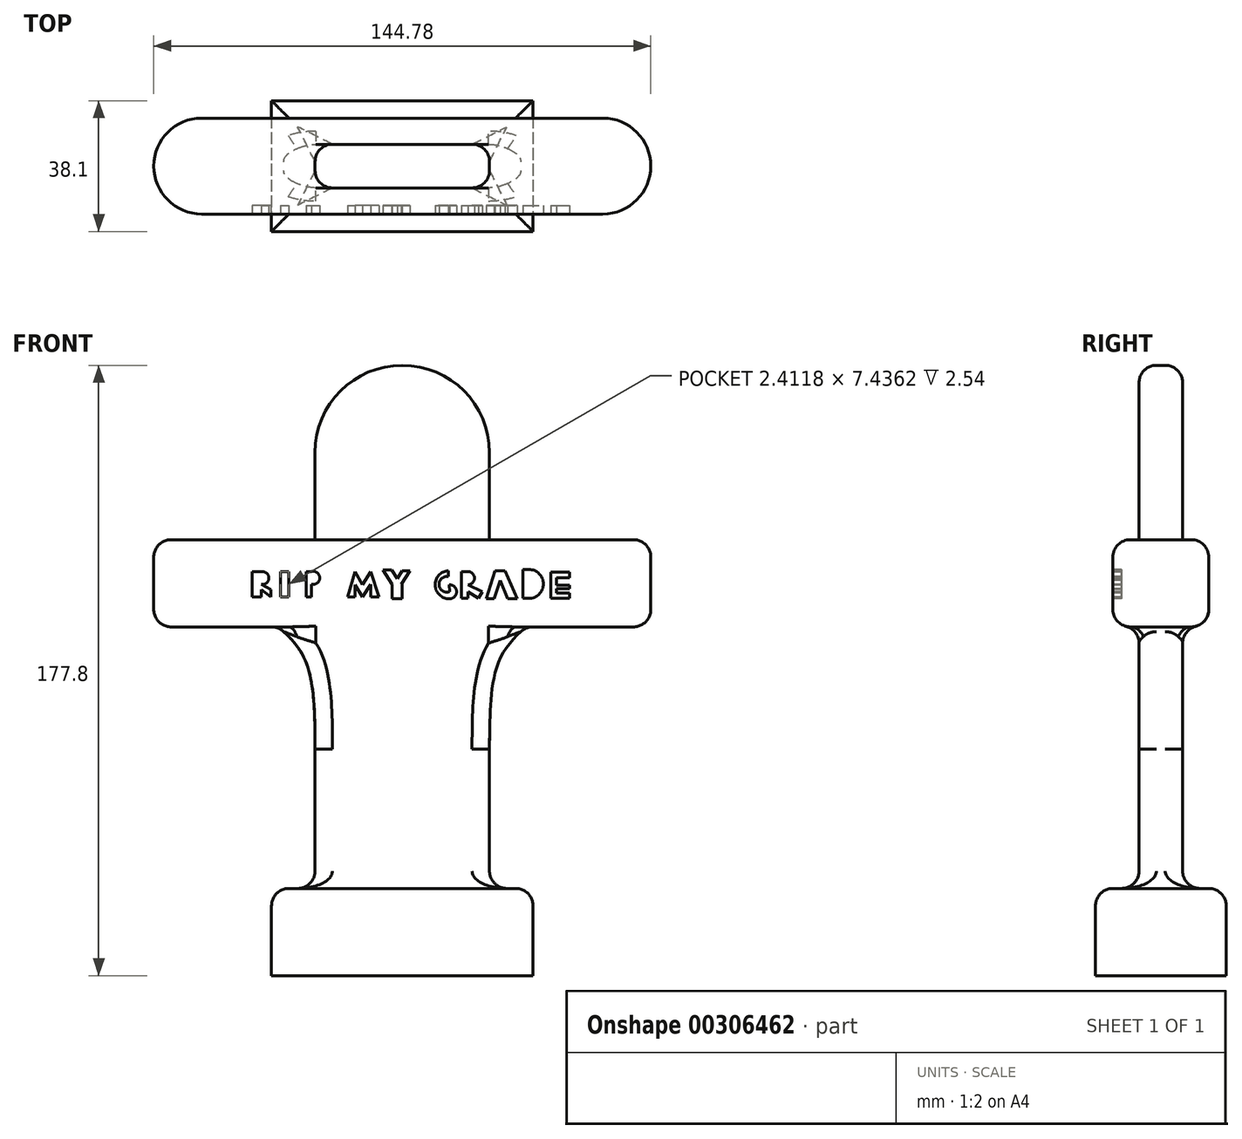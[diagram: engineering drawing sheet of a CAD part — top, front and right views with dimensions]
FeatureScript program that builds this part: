
annotation { "Feature Type Name" : "Feature", "Feature Type Description" : "" }
export const myFeature = defineFeature(function(context is Context, id is Id, definition is map)
    precondition{}
    {
        {
            var Q0;
            Q0=qCreatedBy(makeId("Top.planeOp"),FACE);
            var sketch = newSketch(context, id + "F0", { "sketchPlane" : qUnion([Q0])});
            skLineSegment(sketch, "E0.bottom", {"start": v(-31.32, 7.9) * mm, "end": v(44.88, 7.9) * mm});
            skLineSegment(sketch, "E0.top", {"start": v(-31.32, -30.2) * mm, "end": v(44.88, -30.2) * mm});
            skLineSegment(sketch, "E0.left", {"start": v(-31.32, 7.9) * mm, "end": v(-31.32, -30.2) * mm});
            skLineSegment(sketch, "E0.right", {"start": v(44.88, 7.9) * mm, "end": v(44.88, -30.2) * mm});
            skLineSegment(sketch, "E1", {"start": v(-31.32, -11.15) * mm, "end": v(-18.62, -11.15) * mm, "construction": true});
            skLineSegment(sketch, "E2", {"start": v(-18.62, 7.9) * mm, "end": v(-18.62, -4.8) * mm, "construction": true});
            skLineSegment(sketch, "E3.bottom", {"start": v(-18.62, -4.8) * mm, "end": v(32.18, -4.8) * mm});
            skLineSegment(sketch, "E3.top", {"start": v(-18.62, -17.5) * mm, "end": v(32.18, -17.5) * mm});
            skLineSegment(sketch, "E3.left", {"start": v(-18.62, -4.8) * mm, "end": v(-18.62, -17.5) * mm});
            skLineSegment(sketch, "E3.right", {"start": v(32.18, -4.8) * mm, "end": v(32.18, -17.5) * mm});
            skLineSegment(sketch, "E4", {"start": v(-15.64, -30.2) * mm, "end": v(-15.64, -17.5) * mm, "construction": true});
            skLineSegment(sketch, "E5", {"start": v(32.18, -11.15) * mm, "end": v(44.88, -11.15) * mm, "construction": true});
            skSolve(sketch);
        }
        {
            var Q0;
            Q0=makeQuery(id+"F0.imprint","IMPRINT",FACE,{"disambiguationData":[TD([[makeQuery(id+"F0.imprint","IMPRINT",EDGE,{"derivedFrom":sQuery(id+"F0.wireOp",EDGE,"E0.bottom")}),-1.0]])]});
            extrude(context, id + "F1", {"entities" : qUnion([Q0]), "depth" : 25.4 * mm});
        }
        {
            var Q0;
            Q0=makeQuery(id+"F0.imprint","IMPRINT",FACE,{"disambiguationData":[TD([[makeQuery(id+"F0.imprint","IMPRINT",EDGE,{"derivedFrom":sQuery(id+"F0.wireOp",EDGE,"E3.bottom")}),-1.0]])]});
            extrude(context, id + "F2", {"entities" : qUnion([Q0]), "operationType" : NewBodyOperationType.ADD, "depth" : 101.6 * mm});
        }
        {
            var Q0;
            Q0=makeQuery(id+"F1.opExtrude","CAP_FACE",FACE,{"disambiguationData":[OSD([sQuery(id+"F0.wireOp",EDGE,"E0.bottom"),sQuery(id+"F0.wireOp",EDGE,"E0.top"),sQuery(id+"F0.wireOp",EDGE,"E0.left"),sQuery(id+"F0.wireOp",EDGE,"E0.right"),sQuery(id+"F0.wireOp",EDGE,"E3.bottom"),sQuery(id+"F0.wireOp",EDGE,"E3.top"),sQuery(id+"F0.wireOp",EDGE,"E3.left"),sQuery(id+"F0.wireOp",EDGE,"E3.right")])],"isStart":false});
            fillet(context, id + "F3", {"entities" : qUnion([Q0]), "radius" : 5.08 * mm, "tangentPropagation" : true, "allowEdgeOverflow" : false});
        }
        {
            var Q0;
            Q0=makeQuery(id+"F2.opExtrude","CAP_FACE",FACE,{"disambiguationData":[OSD([sQuery(id+"F0.wireOp",EDGE,"E3.bottom"),sQuery(id+"F0.wireOp",EDGE,"E3.top"),sQuery(id+"F0.wireOp",EDGE,"E3.left"),sQuery(id+"F0.wireOp",EDGE,"E3.right")])],"isStart":false});
            var sketch = newSketch(context, id + "F4", { "sketchPlane" : qUnion([Q0])});
            skLineSegment(sketch, "E6", {"start": v(6.78, -17.5) * mm, "end": v(6.78, -25.12) * mm, "construction": true});
            skLineSegment(sketch, "E7", {"start": v(-18.62, -11.15) * mm, "end": v(-26.24, -11.15) * mm, "construction": true});
            skLineSegment(sketch, "E8.MirrorCS", {"start": v(32.18, -11.15) * mm, "end": v(39.8, -11.15) * mm, "construction": true});
            skLineSegment(sketch, "E9.MirrorCS", {"start": v(6.78, -4.8) * mm, "end": v(6.78, 2.82) * mm, "construction": true});
            skLineSegment(sketch, "E10.bottom", {"start": v(-26.24, -25.12) * mm, "end": v(39.8, -25.12) * mm});
            skLineSegment(sketch, "E10.top", {"start": v(-26.24, 2.82) * mm, "end": v(39.8, 2.82) * mm});
            skLineSegment(sketch, "E10.left", {"start": v(-26.24, -25.12) * mm, "end": v(-26.24, 2.82) * mm});
            skLineSegment(sketch, "E10.right", {"start": v(39.8, -25.12) * mm, "end": v(39.8, 2.82) * mm});
            skSolve(sketch);
        }
        {
            var Q0;
            Q0 = qSketchRegion(id + "F4", true);
            extrude(context, id + "F5", {"entities" : qUnion([Q0]), "operationType" : NewBodyOperationType.ADD, "depth" : 25.4 * mm});
        }
        {
            var Q0;
            Q0=makeQuery(id+"F5.opExtrude","SWEPT_FACE",FACE,{"disambiguationData":[OSD([sQuery(id+"F4.wireOp",EDGE,"E10.right")])]});
            extrude(context, id + "F6", {"entities" : qUnion([Q0]), "operationType" : NewBodyOperationType.ADD, "depth" : 25.4 * mm});
        }
        {
            var Q0;
            Q0=makeQuery(id+"F5.opExtrude","SWEPT_FACE",FACE,{"disambiguationData":[OSD([sQuery(id+"F4.wireOp",EDGE,"E10.left")])]});
            extrude(context, id + "F7", {"entities" : qUnion([Q0]), "operationType" : NewBodyOperationType.ADD, "depth" : 25.4 * mm});
        }
        {
            var Q0;
            {var subQ0=sQuery(id+"F4.wireOp",EDGE,"E10.left");var subQ1=sQuery(id+"F4.wireOp",EDGE,"E10.right");Q0=makeQuery(id+"F7.boolean.opBoolean","MERGE",FACE,{"derivedFrom":[makeQuery(id+"F6.boolean.opBoolean","MERGE",FACE,{"derivedFrom":[makeQuery(id+"F5.opExtrude","CAP_FACE",FACE,{"disambiguationData":[OSD([sQuery(id+"F4.wireOp",EDGE,"E10.bottom"),sQuery(id+"F4.wireOp",EDGE,"E10.top"),subQ0,subQ1])],"isStart":false}),makeQuery(id+"F6.opExtrude","SWEPT_FACE",FACE,{"disambiguationData":[OSD([subQ1]),TDD([makeQuery(id+"F5.opExtrude","CAP_EDGE",EDGE,{"disambiguationData":[OSD([subQ1])],"isStart":false})])]})]}),makeQuery(id+"F7.opExtrude","SWEPT_FACE",FACE,{"disambiguationData":[OSD([subQ0]),TDD([makeQuery(id+"F5.opExtrude","CAP_EDGE",EDGE,{"disambiguationData":[OSD([subQ0])],"isStart":false})])]})]});}
            var sketch = newSketch(context, id + "F8", { "sketchPlane" : qUnion([Q0])});
            skLineSegment(sketch, "E11.0", {"start": v(-18.62, -4.8) * mm, "end": v(32.18, -4.8) * mm});
            skLineSegment(sketch, "E11.1", {"start": v(32.18, -4.8) * mm, "end": v(32.18, -17.5) * mm});
            skLineSegment(sketch, "E11.2", {"start": v(-18.62, -17.5) * mm, "end": v(32.18, -17.5) * mm});
            skLineSegment(sketch, "E11.3", {"start": v(-18.62, -4.8) * mm, "end": v(-18.62, -17.5) * mm});
            skArc(sketch, "E12", {"start": v(65.2, -25.12) * mm, "mid": v(79.17, -11.15) * mm, "end": v(65.2, 2.82) * mm});
            skArc(sketch, "E13", {"start": v(-51.64, 2.82) * mm, "mid": v(-65.6, -11.15) * mm, "end": v(-51.64, -25.12) * mm});
            skSolve(sketch);
        }
        {
            var Q0;
            Q0=makeQuery(id+"F8.imprint","IMPRINT",FACE,{"disambiguationData":[TD([[makeQuery(id+"F8.imprint","IMPRINT",EDGE,{"derivedFrom":sQuery(id+"F8.wireOp",EDGE,"E11.0")}),-1.0]])]});
            extrude(context, id + "F9", {"entities" : qUnion([Q0]), "operationType" : NewBodyOperationType.ADD, "depth" : 25.4 * mm});
        }
        {
            var Q0;
            Q0=makeQuery(id+"F8.imprint","IMPRINT",FACE,{"disambiguationData":[TD([[makeQuery(id+"F8.imprint","IMPRINT",EDGE,{"derivedFrom":sQuery(id+"F8.wireOp",EDGE,"E12")}),1.0]])]});
            var Q1;
            Q1=makeQuery(id+"F8.imprint","IMPRINT",FACE,{"disambiguationData":[TD([[makeQuery(id+"F8.imprint","IMPRINT",EDGE,{"derivedFrom":sQuery(id+"F8.wireOp",EDGE,"E13")}),1.0]])]});
            extrude(context, id + "F10", {"entities" : qUnion([Q0, Q1]), "operationType" : NewBodyOperationType.ADD, "oppositeDirection" : true, "depth" : 25.4 * mm});
        }
        {
            var Q0;
            {var subQ0=sQuery(id+"F4.wireOp",EDGE,"E10.left");var subQ1=sQuery(id+"F4.wireOp",EDGE,"E10.bottom");var subQ2=sQuery(id+"F4.wireOp",EDGE,"E10.right");Q0=makeQuery(id+"F7.boolean.opBoolean","MERGE",EDGE,{"derivedFrom":[makeQuery(id+"F6.boolean.opBoolean","MERGE",EDGE,{"derivedFrom":[makeQuery(id+"F5.opExtrude","CAP_EDGE",EDGE,{"disambiguationData":[OSD([subQ1])],"isStart":true}),makeQuery(id+"F6.opExtrude","SWEPT_EDGE",EDGE,{"disambiguationData":[OSD([subQ1,subQ2]),TDD([makeQuery(id+"F5.opExtrude","CAP_VERTEX",VERTEX,{"disambiguationData":[OSD([subQ1,subQ2])],"isStart":true})])]})]}),makeQuery(id+"F7.opExtrude","SWEPT_EDGE",EDGE,{"disambiguationData":[OSD([subQ1,subQ0]),TDD([makeQuery(id+"F5.opExtrude","CAP_VERTEX",VERTEX,{"disambiguationData":[OSD([subQ1,subQ0])],"isStart":true})])]})]});}
            var Q1;
            {var subQ0=sQuery(id+"F4.wireOp",EDGE,"E10.left");var subQ1=sQuery(id+"F4.wireOp",EDGE,"E10.bottom");var subQ2=sQuery(id+"F4.wireOp",EDGE,"E10.right");Q1=makeQuery(id+"F7.boolean.opBoolean","MERGE",EDGE,{"derivedFrom":[makeQuery(id+"F6.boolean.opBoolean","MERGE",EDGE,{"derivedFrom":[makeQuery(id+"F5.opExtrude","CAP_EDGE",EDGE,{"disambiguationData":[OSD([subQ1])],"isStart":false}),makeQuery(id+"F6.opExtrude","SWEPT_EDGE",EDGE,{"disambiguationData":[OSD([subQ1,subQ2]),TDD([makeQuery(id+"F5.opExtrude","CAP_VERTEX",VERTEX,{"disambiguationData":[OSD([subQ1,subQ2])],"isStart":false})])]})]}),makeQuery(id+"F7.opExtrude","SWEPT_EDGE",EDGE,{"disambiguationData":[OSD([subQ1,subQ0]),TDD([makeQuery(id+"F5.opExtrude","CAP_VERTEX",VERTEX,{"disambiguationData":[OSD([subQ1,subQ0])],"isStart":false})])]})]});}
            var Q2;
            {var subQ0=sQuery(id+"F4.wireOp",EDGE,"E10.left");var subQ1=sQuery(id+"F4.wireOp",EDGE,"E10.top");var subQ2=sQuery(id+"F4.wireOp",EDGE,"E10.right");Q2=makeQuery(id+"F7.boolean.opBoolean","MERGE",EDGE,{"derivedFrom":[makeQuery(id+"F6.boolean.opBoolean","MERGE",EDGE,{"derivedFrom":[makeQuery(id+"F5.opExtrude","CAP_EDGE",EDGE,{"disambiguationData":[OSD([subQ1])],"isStart":false}),makeQuery(id+"F6.opExtrude","SWEPT_EDGE",EDGE,{"disambiguationData":[OSD([subQ1,subQ2]),TDD([makeQuery(id+"F5.opExtrude","CAP_VERTEX",VERTEX,{"disambiguationData":[OSD([subQ1,subQ2])],"isStart":false})])]})]}),makeQuery(id+"F7.opExtrude","SWEPT_EDGE",EDGE,{"disambiguationData":[OSD([subQ1,subQ0]),TDD([makeQuery(id+"F5.opExtrude","CAP_VERTEX",VERTEX,{"disambiguationData":[OSD([subQ1,subQ0])],"isStart":false})])]})]});}
            var Q3;
            {var subQ0=sQuery(id+"F4.wireOp",EDGE,"E10.left");var subQ1=sQuery(id+"F4.wireOp",EDGE,"E10.top");var subQ2=sQuery(id+"F4.wireOp",EDGE,"E10.right");Q3=makeQuery(id+"F7.boolean.opBoolean","MERGE",EDGE,{"derivedFrom":[makeQuery(id+"F6.boolean.opBoolean","MERGE",EDGE,{"derivedFrom":[makeQuery(id+"F5.opExtrude","CAP_EDGE",EDGE,{"disambiguationData":[OSD([subQ1])],"isStart":true}),makeQuery(id+"F6.opExtrude","SWEPT_EDGE",EDGE,{"disambiguationData":[OSD([subQ1,subQ2]),TDD([makeQuery(id+"F5.opExtrude","CAP_VERTEX",VERTEX,{"disambiguationData":[OSD([subQ1,subQ2])],"isStart":true})])]})]}),makeQuery(id+"F7.opExtrude","SWEPT_EDGE",EDGE,{"disambiguationData":[OSD([subQ1,subQ0]),TDD([makeQuery(id+"F5.opExtrude","CAP_VERTEX",VERTEX,{"disambiguationData":[OSD([subQ1,subQ0])],"isStart":true})])]})]});}
            var Q4;
            Q4=makeQuery(id+"F10.opExtrude","CAP_EDGE",EDGE,{"disambiguationData":[OSD([sQuery(id+"F8.wireOp",EDGE,"E12")])],"isStart":true});
            var Q5;
            Q5=makeQuery(id+"F10.opExtrude","CAP_EDGE",EDGE,{"disambiguationData":[OSD([sQuery(id+"F8.wireOp",EDGE,"E13")])],"isStart":true});
            var Q6;
            Q6=makeQuery(id+"F10.opExtrude","CAP_EDGE",EDGE,{"disambiguationData":[OSD([sQuery(id+"F8.wireOp",EDGE,"E13")])],"isStart":false});
            var Q7;
            Q7=makeQuery(id+"F10.opExtrude","CAP_EDGE",EDGE,{"disambiguationData":[OSD([sQuery(id+"F8.wireOp",EDGE,"E12")])],"isStart":false});
            fillet(context, id + "F11", {"entities" : qUnion([Q0, Q1, Q2, Q3, Q4, Q5, Q6, Q7]), "radius" : 5.08 * mm, "tangentPropagation" : true, "allowEdgeOverflow" : false});
        }
        {
            var Q0;
            Q0=makeQuery(id+"F2.opExtrude","SWEPT_FACE",FACE,{"disambiguationData":[OSD([sQuery(id+"F0.wireOp",EDGE,"E3.bottom")])]});
            var sketch = newSketch(context, id + "F12", { "sketchPlane" : qUnion([Q0])});
            skFitSpline(sketch, "E14", {"points": [v(18.62, 66.04) * mm, v(21.3, 91.45) * mm, v(29.6, 101.9) * mm], "startDerivative": vector(0.24, 49.24) * mm, "endDerivative": vector(22.93, 20.98) * mm});
            skLineSegment(sketch, "E15", {"start": v(29.6, 101.9) * mm, "end": v(18.62, 101.6) * mm});
            skLineSegment(sketch, "E16", {"start": v(18.62, 101.6) * mm, "end": v(18.62, 66.04) * mm});
            skLineSegment(sketch, "E17", {"start": v(-6.78, 101.6) * mm, "end": v(-6.78, 30.48) * mm, "construction": true});
            skFitSpline(sketch, "E18.MirrorCS", {"points": [v(-32.18, 66.04) * mm, v(-34.87, 91.45) * mm, v(-43.16, 101.9) * mm], "startDerivative": vector(-0.24, 49.24) * mm, "endDerivative": vector(-22.93, 20.98) * mm});
            skLineSegment(sketch, "E19.MirrorCS", {"start": v(-43.16, 101.9) * mm, "end": v(-32.18, 101.6) * mm});
            skLineSegment(sketch, "E20.MirrorCS", {"start": v(-32.18, 101.6) * mm, "end": v(-32.18, 66.04) * mm});
            skSolve(sketch);
        }
        {
            var Q0;
            Q0=makeQuery(id+"F12.imprint","IMPRINT",FACE,{"disambiguationData":[TD([[makeQuery(id+"F12.imprint","IMPRINT",EDGE,{"derivedFrom":sQuery(id+"F12.wireOp",EDGE,"E18.MirrorCS")}),-1.0]])]});
            var Q1;
            Q1=makeQuery(id+"F12.imprint","IMPRINT",FACE,{"disambiguationData":[TD([[makeQuery(id+"F12.imprint","IMPRINT",EDGE,{"derivedFrom":sQuery(id+"F12.wireOp",EDGE,"E14")}),1.0]])]});
            extrude(context, id + "F13", {"entities" : qUnion([Q0, Q1]), "operationType" : NewBodyOperationType.ADD, "oppositeDirection" : true, "depth" : 12.7 * mm});
        }
        {
            var Q0;
            Q0=makeQuery(id+"F2.opExtrude","SWEPT_EDGE",EDGE,{"disambiguationData":[OSD([sQuery(id+"F0.wireOp",EDGE,"E3.top"),sQuery(id+"F0.wireOp",EDGE,"E3.left")])]});
            var Q1;
            Q1=makeQuery(id+"F2.opExtrude","SWEPT_EDGE",EDGE,{"disambiguationData":[OSD([sQuery(id+"F0.wireOp",EDGE,"E3.top"),sQuery(id+"F0.wireOp",EDGE,"E3.right")])]});
            var Q2;
            Q2=makeQuery(id+"F2.opExtrude","SWEPT_EDGE",EDGE,{"disambiguationData":[OSD([sQuery(id+"F0.wireOp",EDGE,"E3.bottom"),sQuery(id+"F0.wireOp",EDGE,"E3.left")])]});
            var Q3;
            Q3=makeQuery(id+"F2.opExtrude","SWEPT_EDGE",EDGE,{"disambiguationData":[OSD([sQuery(id+"F0.wireOp",EDGE,"E3.bottom"),sQuery(id+"F0.wireOp",EDGE,"E3.right")])]});
            fillet(context, id + "F14", {"entities" : qUnion([Q0, Q1, Q2, Q3]), "radius" : 5.08 * mm, "tangentPropagation" : true, "allowEdgeOverflow" : false});
        }
        {
            var Q0;
            {var subQ0=sQuery(id+"F4.wireOp",EDGE,"E10.bottom");Q0=makeQuery(id+"F7.boolean.opBoolean","MERGE",FACE,{"derivedFrom":[makeQuery(id+"F6.boolean.opBoolean","MERGE",FACE,{"derivedFrom":[makeQuery(id+"F5.opExtrude","SWEPT_FACE",FACE,{"disambiguationData":[OSD([subQ0])]}),makeQuery(id+"F6.opExtrude","SWEPT_FACE",FACE,{"disambiguationData":[OSD([subQ0,sQuery(id+"F4.wireOp",EDGE,"E10.right")])]})]}),makeQuery(id+"F7.opExtrude","SWEPT_FACE",FACE,{"disambiguationData":[OSD([subQ0,sQuery(id+"F4.wireOp",EDGE,"E10.left")])]})]});}
            var sketch = newSketch(context, id + "F15", { "sketchPlane" : qUnion([Q0])});
            skLineSegment(sketch, "E21", {"start": v(-34.32, 110.29) * mm, "end": v(-34.32, 117.67) * mm});
            skArc(sketch, "E22", {"start": v(-34.32, 113.98) * mm, "mid": v(-32.1, 115.82) * mm, "end": v(-34.32, 117.67) * mm});
            skLineSegment(sketch, "E23.bottom", {"start": v(-28.69, 117.73) * mm, "end": v(-26.27, 117.73) * mm});
            skLineSegment(sketch, "E23.top", {"start": v(-28.69, 110.3) * mm, "end": v(-26.27, 110.3) * mm});
            skLineSegment(sketch, "E23.left", {"start": v(-28.69, 117.73) * mm, "end": v(-28.69, 110.3) * mm});
            skLineSegment(sketch, "E23.right", {"start": v(-26.27, 117.73) * mm, "end": v(-26.27, 110.3) * mm});
            skLineSegment(sketch, "E24.bottom", {"start": v(-34.32, 110.29) * mm, "end": v(-36.93, 110.29) * mm});
            skLineSegment(sketch, "E24.top", {"start": v(-34.32, 117.73) * mm, "end": v(-36.93, 117.73) * mm});
            skLineSegment(sketch, "E24.left", {"start": v(-34.32, 110.29) * mm, "end": v(-34.32, 117.73) * mm});
            skLineSegment(sketch, "E24.right", {"start": v(-36.93, 110.29) * mm, "end": v(-36.93, 117.73) * mm});
            skLineSegment(sketch, "E25.bottom", {"start": v(-21.25, 117.73) * mm, "end": v(-19.64, 117.73) * mm});
            skLineSegment(sketch, "E25.top", {"start": v(-21.25, 110.29) * mm, "end": v(-19.64, 110.29) * mm});
            skLineSegment(sketch, "E25.left", {"start": v(-21.25, 117.73) * mm, "end": v(-21.25, 110.29) * mm});
            skLineSegment(sketch, "E25.right", {"start": v(-19.64, 117.73) * mm, "end": v(-19.64, 110.29) * mm});
            skLineSegment(sketch, "E26", {"start": v(-31.5, 110.29) * mm, "end": v(-31.5, 112.5) * mm});
            skLineSegment(sketch, "E27", {"start": v(-31.5, 112.5) * mm, "end": v(-34.32, 113.98) * mm});
            skArc(sketch, "E28", {"start": v(-19.64, 114.01) * mm, "mid": v(-17.25, 115.87) * mm, "end": v(-19.64, 117.73) * mm});
            skLineSegment(sketch, "E29", {"start": v(-9.2, 110.3) * mm, "end": v(-6.98, 117.73) * mm});
            skLineSegment(sketch, "E30", {"start": v(-6.98, 117.73) * mm, "end": v(-4.77, 113.91) * mm});
            skLineSegment(sketch, "E31", {"start": v(-4.77, 113.91) * mm, "end": v(-2.36, 117.73) * mm});
            skLineSegment(sketch, "E32", {"start": v(-2.36, 117.73) * mm, "end": v(0, 110.29) * mm});
            skLineSegment(sketch, "E33", {"start": v(0, 110.29) * mm, "end": v(-2.36, 110.29) * mm});
            skLineSegment(sketch, "E34", {"start": v(-2.36, 110.29) * mm, "end": v(-2.36, 114.01) * mm});
            skPoint(sketch, "E34.endSnap0", {"position": v(-1.18, 114.01) * mm});
            skLineSegment(sketch, "E35", {"start": v(-2.36, 114.01) * mm, "end": v(-4.77, 110.3) * mm});
            skLineSegment(sketch, "E36", {"start": v(-4.77, 110.3) * mm, "end": v(-6.98, 113.91) * mm});
            skLineSegment(sketch, "E37", {"start": v(-9.2, 110.3) * mm, "end": v(-6.98, 110.3) * mm});
            skLineSegment(sketch, "E38", {"start": v(-6.98, 110.3) * mm, "end": v(-6.98, 113.91) * mm});
            skLineSegment(sketch, "E39", {"start": v(1.16, 118.13) * mm, "end": v(3.87, 114.01) * mm});
            skLineSegment(sketch, "E40", {"start": v(3.87, 114.01) * mm, "end": v(6.49, 114.01) * mm});
            skLineSegment(sketch, "E41", {"start": v(6.49, 114.01) * mm, "end": v(8.96, 117.93) * mm});
            skLineSegment(sketch, "E42", {"start": v(8.96, 117.93) * mm, "end": v(6.79, 117.93) * mm});
            skLineSegment(sketch, "E43", {"start": v(6.79, 117.93) * mm, "end": v(5.31, 115.6) * mm});
            skLineSegment(sketch, "E44", {"start": v(5.31, 115.6) * mm, "end": v(3.64, 118.13) * mm});
            skLineSegment(sketch, "E45", {"start": v(3.64, 118.13) * mm, "end": v(1.16, 118.13) * mm});
            skLineSegment(sketch, "E46.bottom", {"start": v(3.87, 114.01) * mm, "end": v(6.69, 114.01) * mm});
            skLineSegment(sketch, "E46.top", {"start": v(3.87, 109.8) * mm, "end": v(6.69, 109.8) * mm});
            skLineSegment(sketch, "E46.left", {"start": v(3.87, 114.01) * mm, "end": v(3.87, 109.8) * mm});
            skLineSegment(sketch, "E46.right", {"start": v(6.69, 114.01) * mm, "end": v(6.69, 109.8) * mm});
            skArc(sketch, "E47", {"start": v(20.25, 117.93) * mm, "mid": v(16.35, 113.71) * mm, "end": v(20.55, 109.8) * mm});
            skArc(sketch, "E48", {"start": v(20.55, 109.8) * mm, "mid": v(22.6, 111.9) * mm, "end": v(20.42, 113.86) * mm});
            skLineSegment(sketch, "E49", {"start": v(20.25, 117.93) * mm, "end": v(20.25, 116.22) * mm});
            skArc(sketch, "E50", {"start": v(20.25, 116.22) * mm, "mid": v(17.49, 113.82) * mm, "end": v(20.56, 111.83) * mm});
            skLineSegment(sketch, "E51", {"start": v(20.42, 113.86) * mm, "end": v(20.56, 111.83) * mm});
            skLineSegment(sketch, "E52.bottom", {"start": v(24.07, 117.73) * mm, "end": v(25.88, 117.73) * mm});
            skLineSegment(sketch, "E52.top", {"start": v(24.07, 110) * mm, "end": v(25.88, 110) * mm});
            skLineSegment(sketch, "E52.left", {"start": v(24.07, 117.73) * mm, "end": v(24.07, 110) * mm});
            skLineSegment(sketch, "E52.right", {"start": v(25.88, 117.73) * mm, "end": v(25.88, 110) * mm});
            skArc(sketch, "E53", {"start": v(25.88, 113.86) * mm, "mid": v(27.82, 115.8) * mm, "end": v(25.88, 117.73) * mm});
            skLineSegment(sketch, "E54", {"start": v(25.88, 111.83) * mm, "end": v(29, 110) * mm});
            skLineSegment(sketch, "E55", {"start": v(29, 110) * mm, "end": v(30.08, 111.83) * mm});
            skLineSegment(sketch, "E56", {"start": v(30.08, 111.83) * mm, "end": v(25.88, 113.86) * mm});
            skLineSegment(sketch, "E57", {"start": v(31.2, 109.8) * mm, "end": v(33.82, 117.93) * mm});
            skLineSegment(sketch, "E58", {"start": v(33.82, 117.93) * mm, "end": v(36.73, 117.93) * mm});
            skLineSegment(sketch, "E59", {"start": v(36.73, 117.93) * mm, "end": v(40.25, 109.8) * mm});
            skLineSegment(sketch, "E60", {"start": v(40.25, 109.8) * mm, "end": v(37.44, 109.8) * mm});
            skLineSegment(sketch, "E61", {"start": v(37.44, 109.8) * mm, "end": v(35.33, 115.12) * mm});
            skLineSegment(sketch, "E62", {"start": v(35.33, 115.12) * mm, "end": v(33.52, 109.8) * mm});
            skLineSegment(sketch, "E63", {"start": v(33.52, 109.8) * mm, "end": v(31.2, 109.8) * mm});
            skLineSegment(sketch, "E64.bottom", {"start": v(41.86, 118.33) * mm, "end": v(43.67, 118.33) * mm});
            skLineSegment(sketch, "E64.top", {"start": v(41.86, 109.9) * mm, "end": v(43.67, 109.9) * mm});
            skLineSegment(sketch, "E64.left", {"start": v(41.86, 118.33) * mm, "end": v(41.86, 109.9) * mm});
            skLineSegment(sketch, "E64.right", {"start": v(43.67, 118.33) * mm, "end": v(43.67, 109.9) * mm});
            skArc(sketch, "E65", {"start": v(43.67, 109.9) * mm, "mid": v(47.89, 114.11) * mm, "end": v(43.67, 118.33) * mm});
            skLineSegment(sketch, "E66.bottom", {"start": v(50.1, 117.53) * mm, "end": v(51.7, 117.53) * mm});
            skLineSegment(sketch, "E66.top", {"start": v(50.1, 110) * mm, "end": v(51.7, 110) * mm});
            skLineSegment(sketch, "E66.left", {"start": v(50.1, 117.53) * mm, "end": v(50.1, 110) * mm});
            skLineSegment(sketch, "E66.right", {"start": v(51.7, 117.53) * mm, "end": v(51.7, 110) * mm});
            skLineSegment(sketch, "E67.bottom", {"start": v(51.7, 110) * mm, "end": v(55.53, 110) * mm});
            skLineSegment(sketch, "E67.top", {"start": v(51.7, 111.4) * mm, "end": v(55.53, 111.4) * mm});
            skLineSegment(sketch, "E67.left", {"start": v(51.7, 110) * mm, "end": v(51.7, 111.4) * mm});
            skLineSegment(sketch, "E67.right", {"start": v(55.53, 110) * mm, "end": v(55.53, 111.4) * mm});
            skLineSegment(sketch, "E68.bottom", {"start": v(51.7, 117.53) * mm, "end": v(55.53, 117.53) * mm});
            skLineSegment(sketch, "E68.top", {"start": v(51.7, 115.92) * mm, "end": v(55.53, 115.92) * mm});
            skLineSegment(sketch, "E68.left", {"start": v(51.7, 117.53) * mm, "end": v(51.7, 115.92) * mm});
            skLineSegment(sketch, "E68.right", {"start": v(55.53, 117.53) * mm, "end": v(55.53, 115.92) * mm});
            skLineSegment(sketch, "E69.bottom", {"start": v(51.7, 113.76) * mm, "end": v(55.53, 113.76) * mm});
            skLineSegment(sketch, "E69.top", {"start": v(51.7, 112.7) * mm, "end": v(55.53, 112.7) * mm});
            skLineSegment(sketch, "E69.left", {"start": v(51.7, 113.76) * mm, "end": v(51.7, 112.7) * mm});
            skLineSegment(sketch, "E69.right", {"start": v(55.53, 113.76) * mm, "end": v(55.53, 112.7) * mm});
            skLineSegment(sketch, "E70", {"start": v(-31.5, 110.29) * mm, "end": v(-34.32, 112.5) * mm});
            skSolve(sketch);
        }
        {
            var Q0;
            {var subQ4=sQuery(id+"F15.wireOp",EDGE,"E24.bottom");Q0=makeQuery(id+"F15.imprint","IMPRINT",FACE,{"disambiguationData":[TD([[makeQuery(id+"F15.imprint","IMPRINT",EDGE,{"derivedFrom":subQ4}),-1.0]])]});}
            var Q1;
            Q1=makeQuery(id+"F15.imprint","IMPRINT",FACE,{"disambiguationData":[TD([[makeQuery(id+"F15.imprint","IMPRINT",EDGE,{"derivedFrom":sQuery(id+"F15.wireOp",EDGE,"YF9r1PJz-NHT6-2BMq-A9CO-P6L6ZAIuONyH")}),1.0]])]});
            var Q2;
            {var subQ0=sQuery(id+"F15.wireOp",EDGE,"E22");Q2=makeQuery(id+"F15.imprint","IMPRINT",FACE,{"disambiguationData":[TD([[makeQuery(id+"F15.imprint","IMPRINT",EDGE,{"derivedFrom":subQ0}),1.0]])]});}
            var Q3;
            Q3=makeQuery(id+"F15.imprint","IMPRINT",FACE,{"disambiguationData":[TD([[makeQuery(id+"F15.imprint","IMPRINT",EDGE,{"derivedFrom":sQuery(id+"F15.wireOp",EDGE,"E23.bottom")}),-1.0]])]});
            var Q4;
            {var subQ2=sQuery(id+"F15.wireOp",EDGE,"E25.bottom");Q4=makeQuery(id+"F15.imprint","IMPRINT",FACE,{"disambiguationData":[TD([[makeQuery(id+"F15.imprint","IMPRINT",EDGE,{"derivedFrom":subQ2}),-1.0]])]});}
            var Q5;
            {var subQ0=sQuery(id+"F15.wireOp",EDGE,"E28");Q5=makeQuery(id+"F15.imprint","IMPRINT",FACE,{"disambiguationData":[TD([[makeQuery(id+"F15.imprint","IMPRINT",EDGE,{"derivedFrom":subQ0}),1.0]])]});}
            var Q6;
            Q6=makeQuery(id+"F15.imprint","IMPRINT",FACE,{"disambiguationData":[TD([[makeQuery(id+"F15.imprint","IMPRINT",EDGE,{"derivedFrom":sQuery(id+"F15.wireOp",EDGE,"E29")}),-1.0]])]});
            var Q7;
            {var subQ1=sQuery(id+"F15.wireOp",EDGE,"E39");Q7=makeQuery(id+"F15.imprint","IMPRINT",FACE,{"disambiguationData":[TD([[makeQuery(id+"F15.imprint","IMPRINT",EDGE,{"derivedFrom":subQ1}),1.0]])]});}
            var Q8;
            Q8=makeQuery(id+"F15.imprint","IMPRINT",FACE,{"disambiguationData":[TD([[makeQuery(id+"F15.imprint","IMPRINT",EDGE,{"derivedFrom":sQuery(id+"F15.wireOp",EDGE,"E46.top")}),1.0]])]});
            var Q9;
            Q9=makeQuery(id+"F15.imprint","IMPRINT",FACE,{"disambiguationData":[TD([[makeQuery(id+"F15.imprint","IMPRINT",EDGE,{"derivedFrom":sQuery(id+"F15.wireOp",EDGE,"E47")}),1.0]])]});
            var Q10;
            {var subQ2=sQuery(id+"F15.wireOp",EDGE,"E52.bottom");Q10=makeQuery(id+"F15.imprint","IMPRINT",FACE,{"disambiguationData":[TD([[makeQuery(id+"F15.imprint","IMPRINT",EDGE,{"derivedFrom":subQ2}),-1.0]])]});}
            var Q11;
            {var subQ2=sQuery(id+"F15.wireOp",EDGE,"E54");Q11=makeQuery(id+"F15.imprint","IMPRINT",FACE,{"disambiguationData":[TD([[makeQuery(id+"F15.imprint","IMPRINT",EDGE,{"derivedFrom":subQ2}),1.0]])]});}
            var Q12;
            {var subQ0=sQuery(id+"F15.wireOp",EDGE,"E53");Q12=makeQuery(id+"F15.imprint","IMPRINT",FACE,{"disambiguationData":[TD([[makeQuery(id+"F15.imprint","IMPRINT",EDGE,{"derivedFrom":subQ0}),1.0]])]});}
            var Q13;
            Q13=makeQuery(id+"F15.imprint","IMPRINT",FACE,{"disambiguationData":[TD([[makeQuery(id+"F15.imprint","IMPRINT",EDGE,{"derivedFrom":sQuery(id+"F15.wireOp",EDGE,"E57")}),-1.0]])]});
            var Q14;
            Q14=makeQuery(id+"F15.imprint","IMPRINT",FACE,{"disambiguationData":[TD([[makeQuery(id+"F15.imprint","IMPRINT",EDGE,{"derivedFrom":sQuery(id+"F15.wireOp",EDGE,"E64.bottom")}),-1.0]])]});
            var Q15;
            Q15=makeQuery(id+"F15.imprint","IMPRINT",FACE,{"disambiguationData":[TD([[makeQuery(id+"F15.imprint","IMPRINT",EDGE,{"derivedFrom":sQuery(id+"F15.wireOp",EDGE,"E64.right")}),1.0]])]});
            var Q16;
            Q16=makeQuery(id+"F15.imprint","IMPRINT",FACE,{"disambiguationData":[TD([[makeQuery(id+"F15.imprint","IMPRINT",EDGE,{"derivedFrom":sQuery(id+"F15.wireOp",EDGE,"E66.bottom")}),-1.0]])]});
            var Q17;
            Q17=makeQuery(id+"F15.imprint","IMPRINT",FACE,{"disambiguationData":[TD([[makeQuery(id+"F15.imprint","IMPRINT",EDGE,{"derivedFrom":sQuery(id+"F15.wireOp",EDGE,"E68.bottom")}),-1.0]])]});
            var Q18;
            Q18=makeQuery(id+"F15.imprint","IMPRINT",FACE,{"disambiguationData":[TD([[makeQuery(id+"F15.imprint","IMPRINT",EDGE,{"derivedFrom":sQuery(id+"F15.wireOp",EDGE,"E69.bottom")}),-1.0]])]});
            var Q19;
            Q19=makeQuery(id+"F15.imprint","IMPRINT",FACE,{"disambiguationData":[TD([[makeQuery(id+"F15.imprint","IMPRINT",EDGE,{"derivedFrom":sQuery(id+"F15.wireOp",EDGE,"E67.bottom")}),1.0]])]});
            var Q20;
            Q20=makeQuery(id+"F15.imprint","IMPRINT",FACE,{"disambiguationData":[TD([[makeQuery(id+"F15.imprint","IMPRINT",EDGE,{"derivedFrom":sQuery(id+"F15.wireOp",EDGE,"E26")}),1.0]])]});
            extrude(context, id + "F16", {"entities" : qUnion([Q0, Q1, Q2, Q3, Q4, Q5, Q6, Q7, Q8, Q9, Q10, Q11, Q12, Q13, Q14, Q15, Q16, Q17, Q18, Q19, Q20]), "operationType" : NewBodyOperationType.REMOVE, "oppositeDirection" : true, "depth" : 2.54 * mm});
        }
        {
            var Q0;
            Q0=makeQuery(id+"F9.opExtrude","SWEPT_FACE",FACE,{"disambiguationData":[OSD([sQuery(id+"F8.wireOp",EDGE,"E11.2")])]});
            var sketch = newSketch(context, id + "F17", { "sketchPlane" : qUnion([Q0])});
            skSolve(sketch);
        }
        {
            var Q0;
            Q0=makeQuery(id+"F9.opExtrude","SWEPT_FACE",FACE,{"disambiguationData":[OSD([sQuery(id+"F8.wireOp",EDGE,"E11.0")])]});
            var sketch = newSketch(context, id + "F18", { "sketchPlane" : qUnion([Q0])});
            skArc(sketch, "E71", {"start": v(18.62, 152.4) * mm, "mid": v(-6.78, 177.8) * mm, "end": v(-32.18, 152.4) * mm});
            skSolve(sketch);
        }
        {
            var Q0;
            Q0=makeQuery(id+"F18.imprint","IMPRINT",FACE,{"disambiguationData":[TD([[makeQuery(id+"F18.imprint","IMPRINT",EDGE,{"derivedFrom":sQuery(id+"F18.wireOp",EDGE,"E71")}),1.0]])]});
            extrude(context, id + "F19", {"entities" : qUnion([Q0]), "operationType" : NewBodyOperationType.ADD, "oppositeDirection" : true, "depth" : 12.7 * mm});
        }
        {
            var Q0;
            Q0=makeQuery(id+"F9.opExtrude","SWEPT_EDGE",EDGE,{"disambiguationData":[OSD([sQuery(id+"F8.wireOp",EDGE,"E11.0"),sQuery(id+"F8.wireOp",EDGE,"E11.3")])]});
            var Q1;
            Q1=makeQuery(id+"F9.opExtrude","SWEPT_EDGE",EDGE,{"disambiguationData":[OSD([sQuery(id+"F8.wireOp",EDGE,"E11.2"),sQuery(id+"F8.wireOp",EDGE,"E11.3")])]});
            fillet(context, id + "F20", {"entities" : qUnion([Q0, Q1]), "radius" : 5.08 * mm, "tangentPropagation" : true, "allowEdgeOverflow" : false});
        }
        {
            var Q0;
            {var subQ0=sQuery(id+"F4.wireOp",EDGE,"E10.left");var subQ1=sQuery(id+"F4.wireOp",EDGE,"E10.right");Q0=makeQuery(id+"F14.opFillet","BLEND_EDGE",EDGE,{"blendedFrom":[makeQuery(id+"F13.opExtrude","CAP_EDGE",EDGE,{"disambiguationData":[OSD([sQuery(id+"F12.wireOp",EDGE,"E18.MirrorCS")])],"isStart":false}),makeQuery(id+"F10.boolean.opBoolean","MERGE",FACE,{"derivedFrom":[makeQuery(id+"F7.boolean.opBoolean","MERGE",FACE,{"derivedFrom":[makeQuery(id+"F6.boolean.opBoolean","MERGE",FACE,{"derivedFrom":[makeQuery(id+"F5.opExtrude","CAP_FACE",FACE,{"disambiguationData":[OSD([sQuery(id+"F4.wireOp",EDGE,"E10.bottom"),sQuery(id+"F4.wireOp",EDGE,"E10.top"),subQ0,subQ1])],"isStart":true}),makeQuery(id+"F6.opExtrude","SWEPT_FACE",FACE,{"disambiguationData":[OSD([subQ1]),TDD([makeQuery(id+"F5.opExtrude","CAP_EDGE",EDGE,{"disambiguationData":[OSD([subQ1])],"isStart":true})])]})]}),makeQuery(id+"F7.opExtrude","SWEPT_FACE",FACE,{"disambiguationData":[OSD([subQ0]),TDD([makeQuery(id+"F5.opExtrude","CAP_EDGE",EDGE,{"disambiguationData":[OSD([subQ0])],"isStart":true})])]})]}),makeQuery(id+"F10.opExtrude","CAP_FACE",FACE,{"disambiguationData":[OSD([subQ1,sQuery(id+"F8.wireOp",EDGE,"E12")])],"isStart":false}),makeQuery(id+"F10.opExtrude","CAP_FACE",FACE,{"disambiguationData":[OSD([subQ0,sQuery(id+"F8.wireOp",EDGE,"E13")])],"isStart":false})]})],"blendedInto":[makeQuery(id+"F10.boolean.opBoolean","MERGE",FACE,{"derivedFrom":[makeQuery(id+"F7.boolean.opBoolean","MERGE",FACE,{"derivedFrom":[makeQuery(id+"F6.boolean.opBoolean","MERGE",FACE,{"derivedFrom":[makeQuery(id+"F5.opExtrude","CAP_FACE",FACE,{"disambiguationData":[OSD([sQuery(id+"F4.wireOp",EDGE,"E10.bottom"),sQuery(id+"F4.wireOp",EDGE,"E10.top"),subQ0,subQ1])],"isStart":true}),makeQuery(id+"F6.opExtrude","SWEPT_FACE",FACE,{"disambiguationData":[OSD([subQ1]),TDD([makeQuery(id+"F5.opExtrude","CAP_EDGE",EDGE,{"disambiguationData":[OSD([subQ1])],"isStart":true})])]})]}),makeQuery(id+"F7.opExtrude","SWEPT_FACE",FACE,{"disambiguationData":[OSD([subQ0]),TDD([makeQuery(id+"F5.opExtrude","CAP_EDGE",EDGE,{"disambiguationData":[OSD([subQ0])],"isStart":true})])]})]}),makeQuery(id+"F10.opExtrude","CAP_FACE",FACE,{"disambiguationData":[OSD([subQ1,sQuery(id+"F8.wireOp",EDGE,"E12")])],"isStart":false}),makeQuery(id+"F10.opExtrude","CAP_FACE",FACE,{"disambiguationData":[OSD([subQ0,sQuery(id+"F8.wireOp",EDGE,"E13")])],"isStart":false})]})]});}
            fillet(context, id + "F21", {"entities" : qUnion([Q0]), "radius" : 5.08 * mm, "tangentPropagation" : true, "allowEdgeOverflow" : false});
        }
        {
            var Q0;
            {var subQ0=sQuery(id+"F8.wireOp",EDGE,"E11.2");Q0=makeQuery(id+"F17.imprint","IMPRINT",FACE,{"disambiguationData":[TD([[makeQuery(id+"F17.imprint","IMPRINT",EDGE,{"derivedFrom":makeQuery(id+"F9.opExtrude","CAP_EDGE",EDGE,{"disambiguationData":[OSD([subQ0])],"isStart":false})}),-1.0]])]});}
            var sketch = newSketch(context, id + "F22", { "sketchPlane" : qUnion([Q0])});
            skLineSegment(sketch, "E72.bottom", {"start": v(-3.54, 149.67) * mm, "end": v(2.94, 149.67) * mm});
            skLineSegment(sketch, "E72.top", {"start": v(-3.54, 143.38) * mm, "end": v(2.94, 143.38) * mm});
            skLineSegment(sketch, "E72.left", {"start": v(-3.54, 149.67) * mm, "end": v(-3.54, 143.38) * mm});
            skLineSegment(sketch, "E72.right", {"start": v(2.94, 149.67) * mm, "end": v(2.94, 143.38) * mm});
            skLineSegment(sketch, "E73.bottom", {"start": v(10.38, 149.48) * mm, "end": v(17.36, 149.48) * mm});
            skLineSegment(sketch, "E73.top", {"start": v(10.38, 142.14) * mm, "end": v(17.36, 142.14) * mm});
            skLineSegment(sketch, "E73.left", {"start": v(10.38, 149.48) * mm, "end": v(10.38, 142.14) * mm});
            skLineSegment(sketch, "E73.right", {"start": v(17.36, 149.48) * mm, "end": v(17.36, 142.14) * mm});
            skArc(sketch, "E74", {"start": v(19.82, 129.96) * mm, "mid": v(7.51, 141.24) * mm, "end": v(-4.58, 129.73) * mm});
            skArc(sketch, "E75", {"start": v(16.64, 129.96) * mm, "mid": v(7.31, 132.72) * mm, "end": v(-1.95, 129.73) * mm});
            skLineSegment(sketch, "E76", {"start": v(-1.95, 129.73) * mm, "end": v(-4.58, 129.73) * mm});
            skLineSegment(sketch, "E77", {"start": v(16.64, 129.96) * mm, "end": v(19.82, 129.96) * mm});
            skSolve(sketch);
        }
        {
            var Q0;
            Q0=makeQuery(id+"F22.imprint","IMPRINT",FACE,{"disambiguationData":[TD([[makeQuery(id+"F22.imprint","IMPRINT",EDGE,{"derivedFrom":sQuery(id+"F22.wireOp",EDGE,"E73.bottom")}),-1.0]])]});
            var Q1;
            Q1=makeQuery(id+"F22.imprint","IMPRINT",FACE,{"disambiguationData":[TD([[makeQuery(id+"F22.imprint","IMPRINT",EDGE,{"derivedFrom":sQuery(id+"F22.wireOp",EDGE,"E74")}),1.0]])]});
            var Q2;
            Q2=makeQuery(id+"F22.imprint","IMPRINT",FACE,{"disambiguationData":[TD([[makeQuery(id+"F22.imprint","IMPRINT",EDGE,{"derivedFrom":sQuery(id+"F22.wireOp",EDGE,"E72.bottom")}),-1.0]])]});
            extrude(context, id + "F23", {"entities" : qUnion([Q0, Q1, Q2]), "operationType" : NewBodyOperationType.ADD, "oppositeDirection" : true, "depth" : 2.54 * mm});
        }
    });
